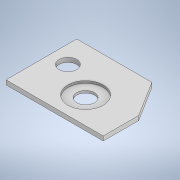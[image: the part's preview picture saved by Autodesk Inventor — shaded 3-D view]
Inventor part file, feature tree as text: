
AUTODESK INVENTOR PART (.ipt)
format: ipt  version: 2022.2 (Build 262287030, 287C)  size: 118,784 bytes
history: native  units: in
note: dims shown in document units (in); Inventor stores cm internally (conversion verified against a paired STEP export)
features: sketch x2, extrude x1, hole x1
ambient origin geometry x8: Origin, YZ Plane, XZ Plane, XY Plane, X Axis, Y Axis, Z Axis, Center Point
bodies: Solid1 (feature_tree)
feature tree (4):
  extrude  "Extrusion1"  Depth=4.0in
  hole  "Hole1"  [1 undecoded]
  sketch  "Sketch1"  dims[d0=2.0in d1=4.0in]
  sketch  "Sketch2"  dims[d2=4.25in d3=5.5in d5=1.0in d6=2.5in d7=1.5in d8=3.0in d9=1.0in d10=0.25in d11=0.0in d12=1.0in d13=0.75in d14=2.0in d15=0.125in d16=0.5635in d17=1.0in d18=0.8108in]
note: 1 required parameter value undecoded (feature->parameter linkage not recoverable at this tier; creation-order binding heuristic only, values carry confidence <= 0.55)
